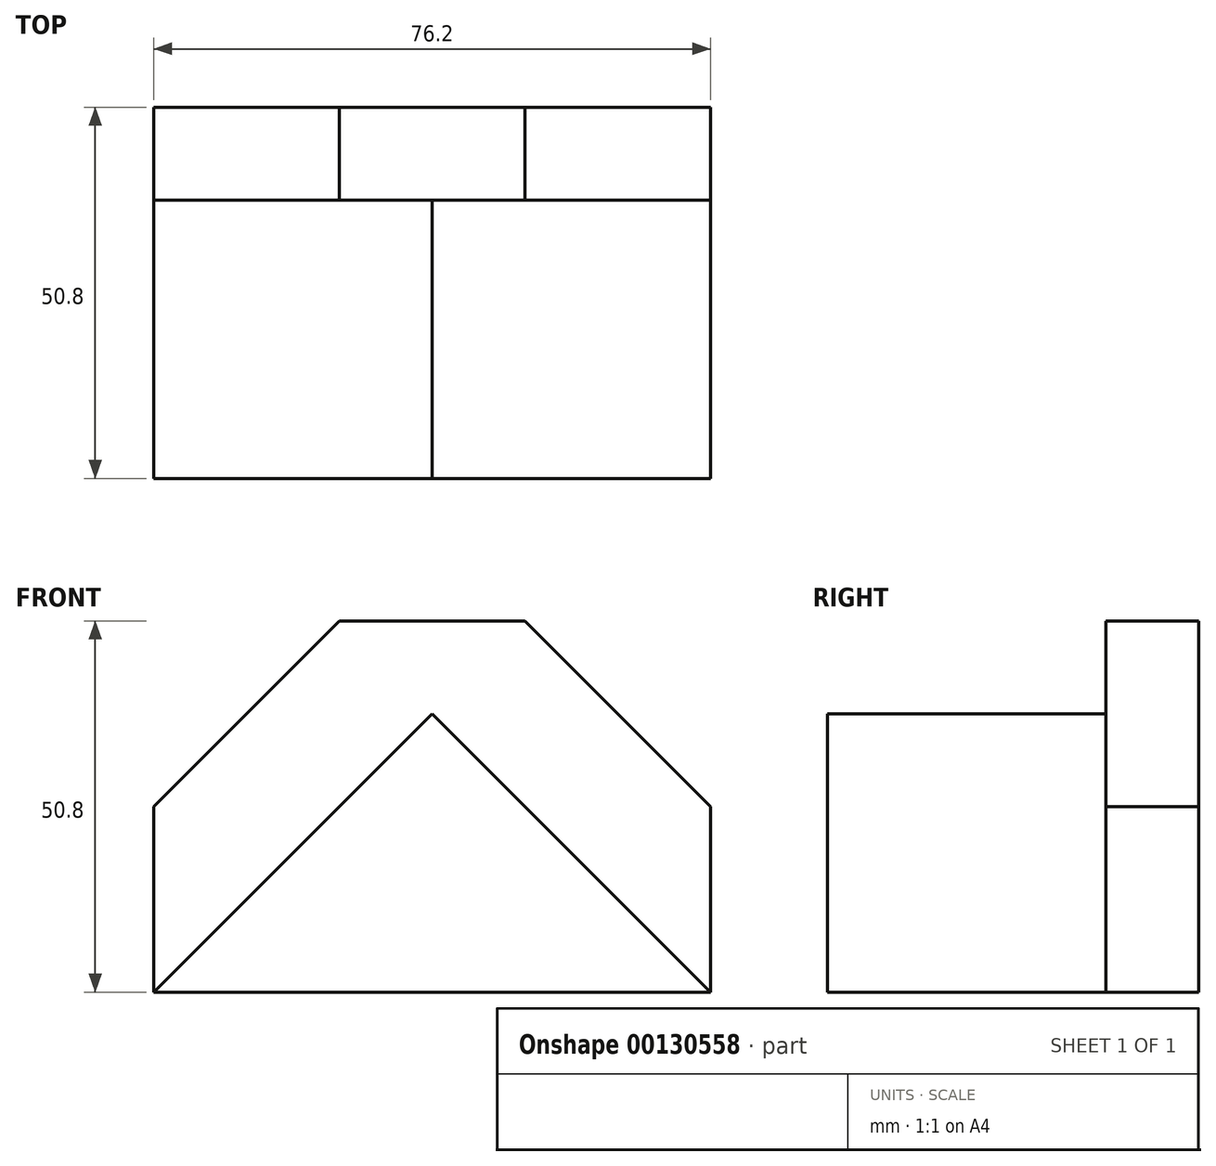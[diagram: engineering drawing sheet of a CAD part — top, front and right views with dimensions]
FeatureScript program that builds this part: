
annotation { "Feature Type Name" : "Feature", "Feature Type Description" : "" }
export const myFeature = defineFeature(function(context is Context, id is Id, definition is map)
    precondition{}
    {
        {
            var Q0;
            Q0=qCreatedBy(makeId("Front.planeOp"),FACE);
            var sketch = newSketch(context, id + "F0", { "sketchPlane" : qUnion([Q0])});
            skLineSegment(sketch, "E0.bottom", {"start": v(0, 0) * mm, "end": v(76.2, 0) * mm});
            skLineSegment(sketch, "E0.top", {"start": v(0, 50.8) * mm, "end": v(76.2, 50.8) * mm});
            skLineSegment(sketch, "E0.left", {"start": v(0, 0) * mm, "end": v(0, 50.8) * mm});
            skLineSegment(sketch, "E0.right", {"start": v(76.2, 0) * mm, "end": v(76.2, 50.8) * mm});
            skLineSegment(sketch, "E1", {"start": v(25.4, 50.8) * mm, "end": v(0, 25.4) * mm});
            skLineSegment(sketch, "E2", {"start": v(50.8, 50.8) * mm, "end": v(76.2, 25.4) * mm});
            skPoint(sketch, "E3.endSnap0", {"position": v(38.1, 50.8) * mm});
            skLineSegment(sketch, "E4", {"start": v(0, 0) * mm, "end": v(38.1, 38.1) * mm});
            skLineSegment(sketch, "E5", {"start": v(38.1, 38.1) * mm, "end": v(76.2, 0) * mm});
            skLineSegment(sketch, "E6", {"start": v(19.05, 0) * mm, "end": v(19.05, 12.7) * mm});
            skLineSegment(sketch, "E7", {"start": v(19.05, 12.7) * mm, "end": v(57.15, 12.7) * mm});
            skLineSegment(sketch, "E8", {"start": v(57.15, 12.7) * mm, "end": v(57.15, 0) * mm});
            skLineSegment(sketch, "E9", {"start": v(25.4, 50.8) * mm, "end": v(50.8, 50.8) * mm});
            skLineSegment(sketch, "E10", {"start": v(0, 25.4) * mm, "end": v(0, 0) * mm});
            skLineSegment(sketch, "E11", {"start": v(76.2, 25.4) * mm, "end": v(76.2, 0) * mm});
            skLineSegment(sketch, "E12", {"start": v(76.2, 0) * mm, "end": v(0, 0) * mm});
            skSolve(sketch);
        }
        {
            var Q0;
            Q0=makeQuery(id+"F0.imprint","IMPRINT",FACE,{"disambiguationData":[TD([[makeQuery(id+"F0.imprint","IMPRINT",EDGE,{"derivedFrom":sQuery(id+"F0.wireOp",EDGE,"E1")}),1.0]])]});
            var Q1;
            {var subQ4=sQuery(id+"F0.wireOp",EDGE,"E4");Q1=makeQuery(id+"F0.imprint","IMPRINT",FACE,{"disambiguationData":[TD([[makeQuery(id+"F0.imprint","IMPRINT",EDGE,{"derivedFrom":subQ4}),-1.0]])]});}
            var Q2;
            {var subQ0=sQuery(id+"F0.wireOp",EDGE,"E6");Q2=makeQuery(id+"F0.imprint","IMPRINT",FACE,{"disambiguationData":[TD([[makeQuery(id+"F0.imprint","IMPRINT",EDGE,{"derivedFrom":subQ0}),-1.0]])]});}
            extrude(context, id + "F1", {"entities" : qUnion([Q0, Q1, Q2]), "oppositeDirection" : true, "depth" : 50.8 * mm});
        }
        {
            var Q0;
            Q0=makeQuery(id+"F0.imprint","IMPRINT",FACE,{"disambiguationData":[TD([[makeQuery(id+"F0.imprint","IMPRINT",EDGE,{"derivedFrom":sQuery(id+"F0.wireOp",EDGE,"E1")}),1.0]])]});
            extrude(context, id + "F2", {"entities" : qUnion([Q0]), "operationType" : NewBodyOperationType.REMOVE, "oppositeDirection" : true, "depth" : 38.1 * mm});
        }
    });
